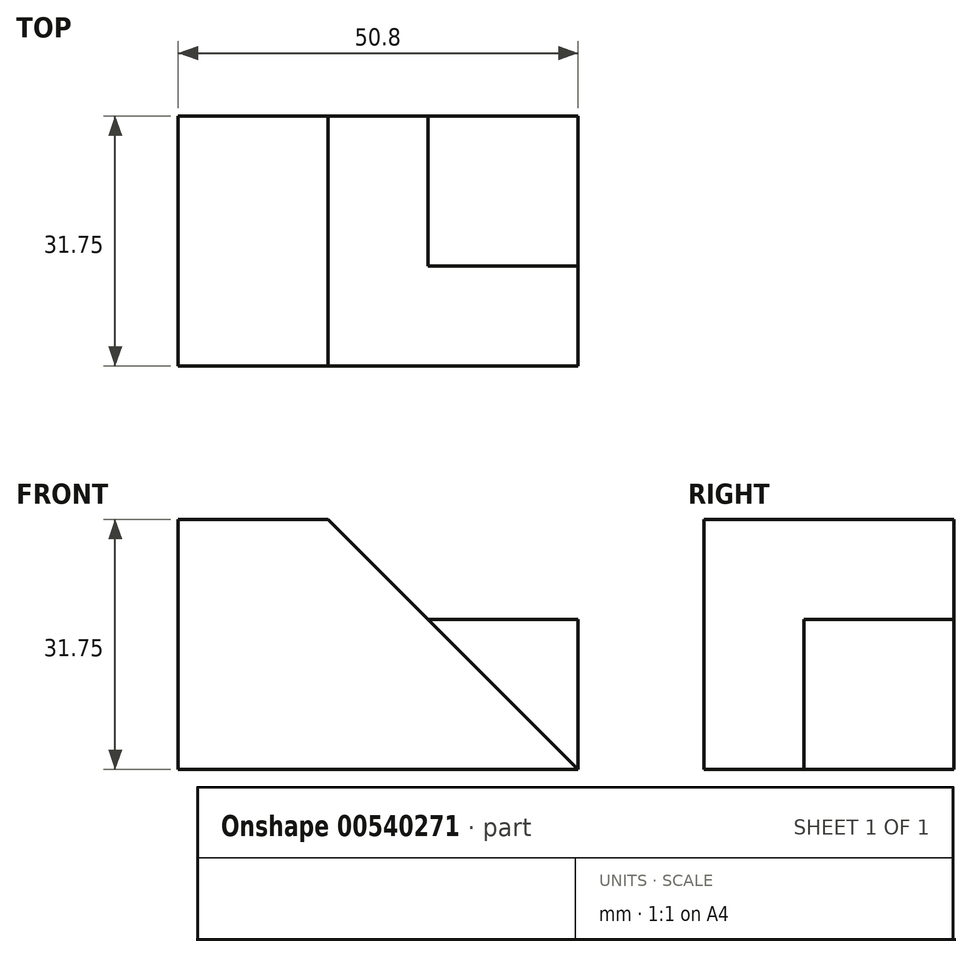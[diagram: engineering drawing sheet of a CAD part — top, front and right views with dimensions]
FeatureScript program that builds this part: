
annotation { "Feature Type Name" : "Feature", "Feature Type Description" : "" }
export const myFeature = defineFeature(function(context is Context, id is Id, definition is map)
    precondition{}
    {
        {
            var Q0;
            Q0=qCreatedBy(makeId("Front.planeOp"),FACE);
            var sketch = newSketch(context, id + "F0", { "sketchPlane" : qUnion([Q0])});
            skLineSegment(sketch, "E0", {"start": v(-18.7, 27.47) * mm, "end": v(-37.75, 27.47) * mm});
            skLineSegment(sketch, "E1", {"start": v(-37.75, 27.47) * mm, "end": v(-37.75, -4.28) * mm});
            skLineSegment(sketch, "E2", {"start": v(-37.75, -4.28) * mm, "end": v(13.05, -4.28) * mm});
            skLineSegment(sketch, "E3", {"start": v(13.05, -4.28) * mm, "end": v(-18.7, 27.47) * mm});
            skSolve(sketch);
        }
        {
            var Q0;
            Q0=makeQuery(id+"F0.imprint","IMPRINT",FACE,{"disambiguationData":[TD([[makeQuery(id+"F0.imprint","IMPRINT",EDGE,{"derivedFrom":sQuery(id+"F0.wireOp",EDGE,"E0")}),1.0]])]});
            extrude(context, id + "F1", {"entities" : qUnion([Q0]), "depth" : 31.75 * mm, "offsetDistance" : 25.4 * mm});
        }
        {
            var Q0;
            Q0=makeQuery(id+"F1.opExtrude","CAP_FACE",FACE,{"disambiguationData":[OSD([sQuery(id+"F0.wireOp",EDGE,"E0"),sQuery(id+"F0.wireOp",EDGE,"E1"),sQuery(id+"F0.wireOp",EDGE,"E2"),sQuery(id+"F0.wireOp",EDGE,"E3")])],"isStart":true});
            var sketch = newSketch(context, id + "F2", { "sketchPlane" : qUnion([Q0])});
            skLineSegment(sketch, "E4", {"start": v(-13.05, -4.28) * mm, "end": v(-13.05, 14.77) * mm});
            skLineSegment(sketch, "E5", {"start": v(-13.05, 14.77) * mm, "end": v(6, 14.77) * mm});
            skSolve(sketch);
        }
        {
            var Q0;
            {var subQ0=sQuery(id+"F2.wireOp",EDGE,"E4");Q0=makeQuery(id+"F2.imprint","IMPRINT",FACE,{"disambiguationData":[TD([[makeQuery(id+"F2.imprint","IMPRINT",EDGE,{"derivedFrom":subQ0}),-1.0]])]});}
            extrude(context, id + "F3", {"entities" : qUnion([Q0]), "operationType" : NewBodyOperationType.ADD, "oppositeDirection" : true, "depth" : 19.05 * mm, "offsetDistance" : 25.4 * mm});
        }
    });
